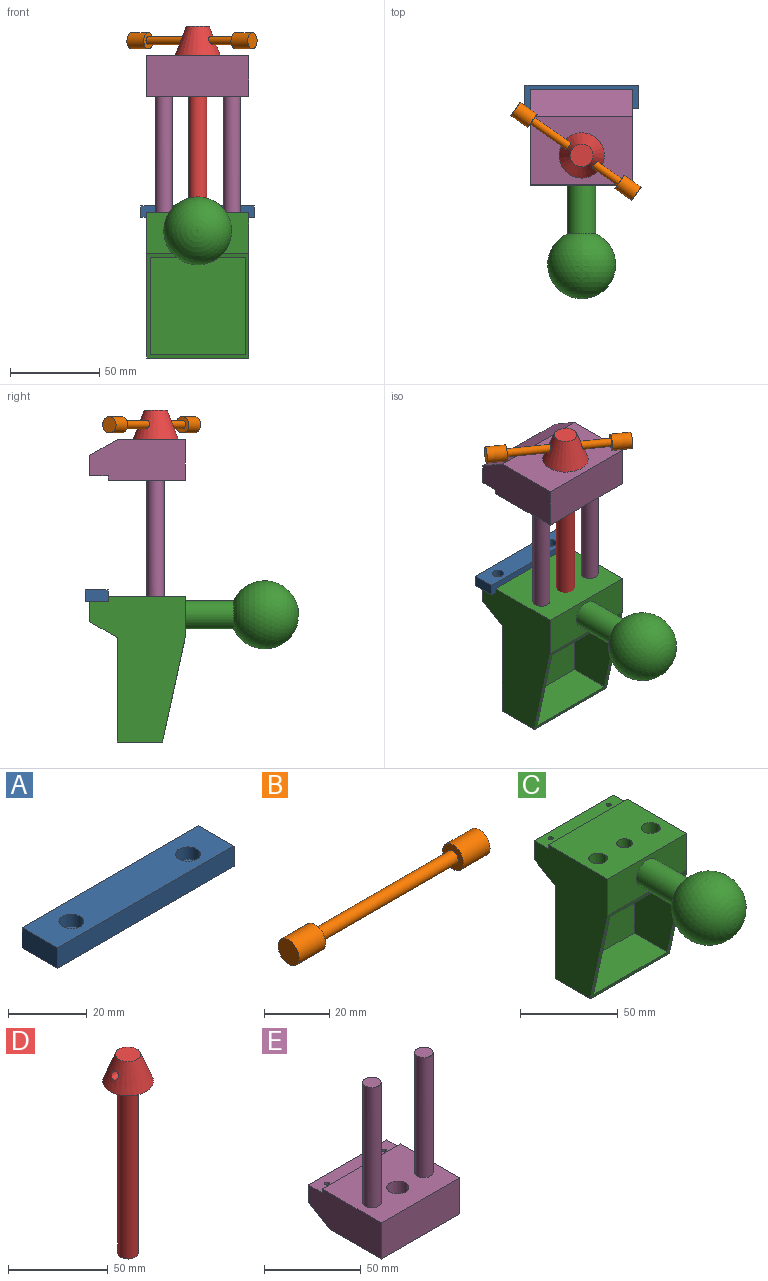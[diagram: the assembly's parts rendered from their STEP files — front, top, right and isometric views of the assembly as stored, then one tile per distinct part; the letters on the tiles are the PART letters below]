
ASSEMBLY  parts=5 mates=7
PART A: 12 faces, bbox 63.5x12.7x6.4 mm
  f0: plane 12.7x6.35mm, normal (1,0,0), area 80.6mm2, adj f1,f3,f4,f5
  f1: plane 63.5x6.35mm, normal (0,1,0), area 403.2mm2, adj f0,f2,f4,f5
  f2: plane 12.7x6.35mm, normal (-1,0,0), area 80.6mm2, adj f1,f3,f4,f5
  f3: plane 63.5x6.35mm, normal (0,-1,0), area 403.2mm2, adj f0,f2,f4,f5
  f4: plane 63.5x12.7mm, normal (0,0,1), area 743.1mm2, adj f0,f1,f2,f3,f8,f11
  f5: plane 63.5x12.7mm, normal (0,0,-1), area 780.5mm2, adj f0,f1,f2,f3,f6,f9
  f6: cylinder r=2.03mm len=4.06mm, axis (0,0,1), area 32.4mm2, adj f5,f7
  f7: plane 6.35x6.35mm, normal (0,0,1), area 18.7mm2, adj f6,f8
  f8: cylinder r=3.17mm len=6.35mm, axis (0,0,1), area 76mm2, adj f4,f7
  f9: cylinder r=2.03mm len=4.06mm, axis (0,0,1), area 32.4mm2, adj f5,f10
  f10: plane 6.35x6.35mm, normal (0,0,1), area 18.7mm2, adj f9,f11
  f11: cylinder r=3.17mm len=6.35mm, axis (0,0,1), area 76mm2, adj f4,f10
PART B: 7 faces, bbox 82.6x9.1x9.1 mm
  f0: plane 9.14x9.14mm, normal (-1,0,0), area 65.7mm2, adj f1
  f1: cylinder r=4.57mm len=11.43mm, axis (-1,0,0), area 328.3mm2, adj f0,f2
  f2: plane 9.14x9.14mm, normal (1,0,0), area 49.3mm2, adj f1,f3
  f3: cylinder r=2.29mm len=59.69mm, axis (-1,0,0), area 857.3mm2, adj f2,f4
  f4: plane 9.14x9.14mm, normal (-1,0,0), area 49.3mm2, adj f3,f5
  f5: cylinder r=4.57mm len=11.43mm, axis (-1,0,0), area 328.3mm2, adj f4,f6
  f6: plane 9.14x9.14mm, normal (1,0,0), area 65.7mm2, adj f5
PART C: 25 faces, bbox 57.2x116.8x90.2 mm
  f0: plane 57.15x43.18mm, normal (0,0,1), area 2275.7mm2, adj f1,f2,f9,f10,f18,f19,f20
  f1: plane 57.15x2.54mm, normal (0,1,0), area 145.2mm2, adj f0,f8,f9,f10
  f2: plane 57.15x22.86mm, normal (0,-1,0), area 1108.5mm2, adj f0,f3,f9,f10,f12
  f3: plane 58.42x57.15mm, normal (0,-0.98,-0.21), area 435.8mm2, adj f2,f4,f9,f10,f13,f14,f15,f16
  f4: plane 57.15x25.4mm, normal (0,0,-1), area 1451.6mm2, adj f3,f5,f9,f10
  f5: plane 58.42x57.15mm, normal (0,1,0), area 3338.7mm2, adj f4,f6,f9,f10
  f6: plane 57.15x15.24mm, normal (0,0.5,-0.86), area 1008.3mm2, adj f5,f7,f9,f10
  f7: plane 57.15x11.43mm, normal (0,1,0), area 653.2mm2, adj f6,f8,f9,f10
  f8: plane 57.15x10.16mm, normal (0,0,1), area 570.2mm2, adj f1,f7,f9,f10,f22,f24
  f9: plane 81.28x53.34mm, normal (1,0,0), area 2980.6mm2, adj f0,f1,f2,f3,f4,f5,f6,f7
  f10: plane 81.28x53.34mm, normal (-1,0,0), area 2980.6mm2, adj f0,f1,f2,f3,f4,f5,f6,f7
  f11: sphere r=19.05mm, area 4353mm2, adj f12
  f12: cylinder r=7.94mm len=27.13mm, axis (0,1,0), area 1353.2mm2, adj f2,f11
  f13: plane 53.34x23.91mm, normal (0,0,1), area 1275.3mm2, adj f3,f14,f16,f17
  f14: plane 54.61x35.78mm, normal (-1,0,0), area 1629.8mm2, adj f3,f13,f15,f17
  f15: plane 53.34x35.78mm, normal (0,0,-1), area 1716.6mm2, adj f3,f14,f16,f17,f18,f19,f20
  f16: plane 54.61x35.78mm, normal (1,0,0), area 1629.8mm2, adj f3,f13,f15,f17
  f17: plane 54.61x53.34mm, normal (0,-1,0), area 2912.9mm2, adj f13,f14,f15,f16
  f18: cylinder r=4.76mm len=24.77mm, axis (0,0,1), area 741.1mm2, adj f0,f15
  f19: cylinder r=4.76mm len=24.77mm, axis (0,0,1), area 741.1mm2, adj f0,f15
  f20: cylinder r=3.97mm len=24.77mm, axis (0,0,1), area 617.5mm2, adj f0,f15
  f21: cone r=1.29mm half-angle=59deg, axis (0,0,1), area 6.1mm2, adj f22
  f22: cylinder r=1.29mm len=5.08mm, axis (0,0,1), area 41.1mm2, adj f8,f21
  f23: cone r=1.29mm half-angle=59deg, axis (0,0,1), area 6.1mm2, adj f24
  f24: cylinder r=1.29mm len=5.08mm, axis (0,0,1), area 41.1mm2, adj f8,f23
PART D: 6 faces, bbox 25.4x25.4x121.9 mm
  f0: cone r=12.7mm half-angle=21deg, axis (0,0,-1), area 1023.2mm2, adj f1,f2,f5
  f1: plane 12.7x12.7mm, normal (0,0,1), area 126.7mm2, adj f0
  f2: plane 25.4x25.4mm, normal (0,0,-1), area 425.6mm2, adj f0,f3
  f3: cylinder r=5.08mm len=105.41mm, axis (0,0,1), area 3364.5mm2, adj f2,f4
  f4: plane 10.16x10.16mm, normal (0,0,-1), area 81.1mm2, adj f3
  f5: cylinder r=2.29mm len=20.81mm, axis (-1,0,0), area 269.6mm2, adj f0
PART E: 18 faces, bbox 57.2x53.3x99.1 mm
  f0: plane 57.15x43.18mm, normal (0,0,1), area 2222.6mm2, adj f1,f6,f7,f8,f13,f14,f16
  f1: plane 57.15x22.86mm, normal (0,-1,0), area 1306.4mm2, adj f0,f2,f7,f8
  f2: plane 57.15x38.1mm, normal (0,0,-1), area 2074.8mm2, adj f1,f3,f7,f8,f13
  f3: plane 57.15x15.24mm, normal (0,0.5,-0.86), area 1008.3mm2, adj f2,f4,f7,f8
  f4: plane 57.15x11.43mm, normal (0,1,0), area 653.2mm2, adj f3,f5,f7,f8
  f5: plane 57.15x10.16mm, normal (0,0,1), area 570.2mm2, adj f4,f6,f7,f8,f10,f12
  f6: plane 57.15x2.54mm, normal (0,1,0), area 145.2mm2, adj f0,f5,f7,f8
  f7: plane 53.34x22.86mm, normal (1,0,0), area 1125.8mm2, adj f0,f1,f2,f3,f4,f5,f6
  f8: plane 53.34x22.86mm, normal (-1,0,0), area 1125.8mm2, adj f0,f1,f2,f3,f4,f5,f6
  f9: cone r=1.29mm half-angle=59deg, axis (0,0,1), area 6.1mm2, adj f10
  f10: cylinder r=1.29mm len=5.08mm, axis (0,0,1), area 41.1mm2, adj f5,f9
  f11: cone r=1.29mm half-angle=59deg, axis (0,0,1), area 6.1mm2, adj f12
  f12: cylinder r=1.29mm len=5.08mm, axis (0,0,1), area 41.1mm2, adj f5,f11
  f13: cylinder r=5.71mm len=22.86mm, axis (0,0,1), area 820.9mm2, adj f0,f2
  f14: cylinder r=4.76mm len=76.2mm, axis (0,0,-1), area 2280.2mm2, adj f0,f15
  f15: plane 9.53x9.53mm, normal (0,0,1), area 71.3mm2, adj f14
  f16: cylinder r=4.76mm len=76.2mm, axis (0,0,-1), area 2280.2mm2, adj f0,f17
  f17: plane 9.53x9.53mm, normal (0,0,1), area 71.3mm2, adj f16
PLACE A t=(-86.29,-7.72,70.56)mm
PLACE B rot(axis=(-0.83,0.26,-0.49),65.5deg) t=(-87.45,-55.84,169.39)mm
PLACE C t=(-118.04,-34.39,73.1)mm fixed
PLACE D rot(axis=(0,0,-1),35deg) t=(-118.04,-34.39,161.13)mm
PLACE E rot(axis=(0,-1,0),180deg) t=(-118.04,-34.39,138.27)mm
MATE cylindrical E.f16 <-> C.f19  axis (0,0,1) through (-137.09,-34.39,62.07)mm
MATE cylindrical E.f14 <-> C.f18  axis (0,0,1) through (-98.99,-34.39,100.17)mm
MATE cylindrical C.f23 <-> A.f9  axis (0,0,1) through (-139,-2.01,70.56)mm
MATE cylindrical B.f1 <-> D.f5  axis (-0.82,0.57,0) through (-121.24,-32.15,169.39)mm
MATE planar C.f8 <-> A.f5  axis (0,0,1) through (-118.04,-2.65,70.56)mm
MATE cylindrical C.f21 <-> A.f6  axis (0,0,1) through (-97.09,-2.01,70.56)mm
MATE revolute D.f0 <-> E.f13  axis (0,0,-1) through (-118.04,-34.39,161.13)mm
